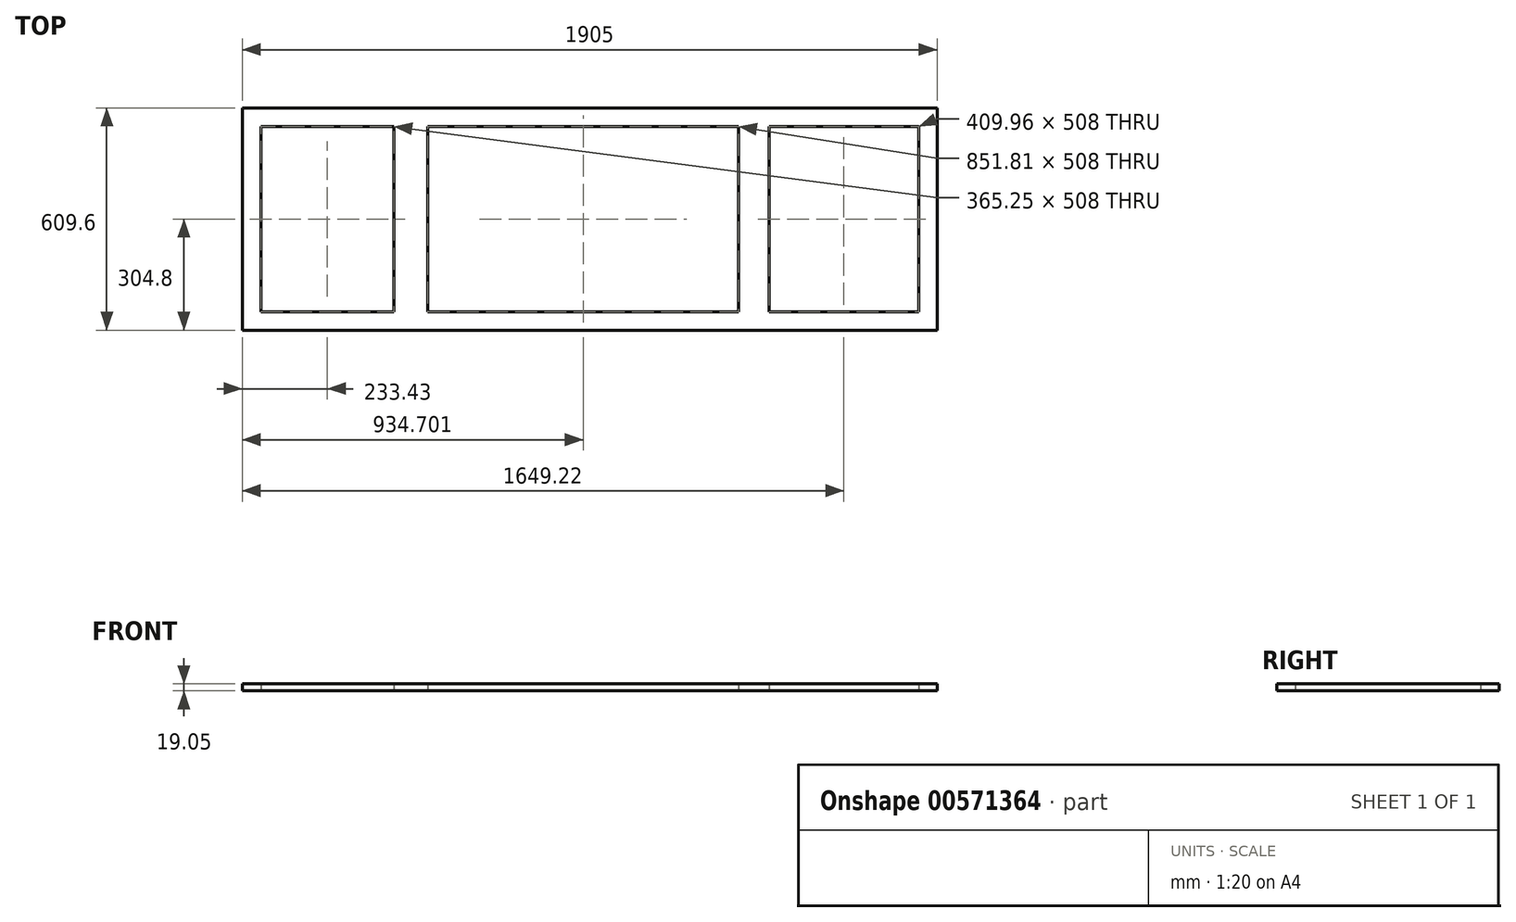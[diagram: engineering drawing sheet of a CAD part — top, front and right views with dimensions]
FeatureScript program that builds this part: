
annotation { "Feature Type Name" : "Feature", "Feature Type Description" : "" }
export const myFeature = defineFeature(function(context is Context, id is Id, definition is map)
    precondition{}
    {
        {
            var Q0;
            Q0=qCreatedBy(makeId("Top.planeOp"),FACE);
            var sketch = newSketch(context, id + "F0", { "sketchPlane" : qUnion([Q0])});
            skLineSegment(sketch, "E0", {"start": v(-940.37, 50.8) * mm, "end": v(964.63, 50.8) * mm});
            skLineSegment(sketch, "E1", {"start": v(-940.37, 50.8) * mm, "end": v(-940.37, 0) * mm});
            skLineSegment(sketch, "E2", {"start": v(-940.37, 0) * mm, "end": v(964.63, 0) * mm});
            skLineSegment(sketch, "E3", {"start": v(964.63, 0) * mm, "end": v(964.63, 50.8) * mm});
            skSolve(sketch);
        }
        {
            var Q0;
            Q0=makeQuery(id+"F0.imprint","IMPRINT",FACE,{"disambiguationData":[TD([[makeQuery(id+"F0.imprint","IMPRINT",EDGE,{"derivedFrom":sQuery(id+"F0.wireOp",EDGE,"E0")}),-1.0]])]});
            extrude(context, id + "F1", {"entities" : qUnion([Q0]), "depth" : 19.05 * mm, "offsetDistance" : 25.4 * mm});
        }
        {
            var Q0;
            Q0=makeQuery(id+"F1.opExtrude","SWEPT_FACE",FACE,{"disambiguationData":[OSD([sQuery(id+"F0.wireOp",EDGE,"E2")])]});
            var sketch = newSketch(context, id + "F2", { "sketchPlane" : qUnion([Q0])});
            skLineSegment(sketch, "E4.bottom", {"start": v(-940.37, 19.05) * mm, "end": v(-889.57, 19.05) * mm});
            skLineSegment(sketch, "E4.top", {"start": v(-940.37, 0) * mm, "end": v(-889.57, 0) * mm});
            skLineSegment(sketch, "E4.left", {"start": v(-940.37, 19.05) * mm, "end": v(-940.37, 0) * mm});
            skLineSegment(sketch, "E4.right", {"start": v(-889.57, 19.05) * mm, "end": v(-889.57, 0) * mm});
            skLineSegment(sketch, "E5.bottom", {"start": v(964.63, 19.05) * mm, "end": v(913.83, 19.05) * mm});
            skLineSegment(sketch, "E5.top", {"start": v(964.63, 0) * mm, "end": v(913.83, 0) * mm});
            skLineSegment(sketch, "E5.left", {"start": v(964.63, 19.05) * mm, "end": v(964.63, 0) * mm});
            skLineSegment(sketch, "E5.right", {"start": v(913.83, 19.05) * mm, "end": v(913.83, 0) * mm});
            skSolve(sketch);
        }
        {
            var Q0;
            Q0=makeQuery(id+"F2.imprint","IMPRINT",FACE,{"disambiguationData":[TD([[makeQuery(id+"F2.imprint","IMPRINT",EDGE,{"derivedFrom":sQuery(id+"F2.wireOp",EDGE,"E4.bottom")}),-1.0]])]});
            var Q1;
            Q1=makeQuery(id+"F2.imprint","IMPRINT",FACE,{"disambiguationData":[TD([[makeQuery(id+"F2.imprint","IMPRINT",EDGE,{"derivedFrom":sQuery(id+"F2.wireOp",EDGE,"E5.bottom")}),-1.0]])]});
            extrude(context, id + "F3", {"entities" : qUnion([Q0, Q1]), "operationType" : NewBodyOperationType.ADD, "depth" : 558.8 * mm, "offsetDistance" : 25.4 * mm});
        }
        {
            var Q0;
            Q0=makeQuery(id+"F3.opExtrude","SWEPT_FACE",FACE,{"disambiguationData":[OSD([sQuery(id+"F2.wireOp",EDGE,"E4.right")])]});
            var sketch = newSketch(context, id + "F4", { "sketchPlane" : qUnion([Q0])});
            skLineSegment(sketch, "E6.bottom", {"start": v(-558.8, 19.05) * mm, "end": v(-508, 19.05) * mm});
            skLineSegment(sketch, "E6.top", {"start": v(-558.8, 0) * mm, "end": v(-508, 0) * mm});
            skLineSegment(sketch, "E6.left", {"start": v(-558.8, 19.05) * mm, "end": v(-558.8, 0) * mm});
            skLineSegment(sketch, "E6.right", {"start": v(-508, 19.05) * mm, "end": v(-508, 0) * mm});
            skSolve(sketch);
        }
        {
            var Q0;
            Q0=makeQuery(id+"F4.imprint","IMPRINT",FACE,{"disambiguationData":[TD([[makeQuery(id+"F4.imprint","IMPRINT",EDGE,{"derivedFrom":sQuery(id+"F4.wireOp",EDGE,"E6.bottom")}),-1.0]])]});
            extrude(context, id + "F5", {"entities" : qUnion([Q0]), "operationType" : NewBodyOperationType.ADD, "depth" : 1854.2 * mm, "offsetDistance" : 25.4 * mm});
        }
        {
            var Q0;
            Q0=makeQuery(id+"F1.opExtrude","SWEPT_FACE",FACE,{"disambiguationData":[OSD([sQuery(id+"F0.wireOp",EDGE,"E2")])]});
            var sketch = newSketch(context, id + "F6", { "sketchPlane" : qUnion([Q0])});
            skLineSegment(sketch, "E7.bottom", {"start": v(-524.31, 19.05) * mm, "end": v(-431.58, 19.05) * mm});
            skLineSegment(sketch, "E7.top", {"start": v(-524.31, 0) * mm, "end": v(-431.58, 0) * mm});
            skLineSegment(sketch, "E7.left", {"start": v(-524.31, 19.05) * mm, "end": v(-524.31, 0) * mm});
            skLineSegment(sketch, "E7.right", {"start": v(-431.58, 19.05) * mm, "end": v(-431.58, 0) * mm});
            skLineSegment(sketch, "E8.bottom", {"start": v(420.24, 19.05) * mm, "end": v(503.87, 19.05) * mm});
            skLineSegment(sketch, "E8.top", {"start": v(420.24, 0) * mm, "end": v(503.87, 0) * mm});
            skLineSegment(sketch, "E8.left", {"start": v(420.24, 19.05) * mm, "end": v(420.24, 0) * mm});
            skLineSegment(sketch, "E8.right", {"start": v(503.87, 19.05) * mm, "end": v(503.87, 0) * mm});
            skSolve(sketch);
        }
        {
            var Q0;
            Q0=makeQuery(id+"F6.imprint","IMPRINT",FACE,{"disambiguationData":[TD([[makeQuery(id+"F6.imprint","IMPRINT",EDGE,{"derivedFrom":sQuery(id+"F6.wireOp",EDGE,"E8.bottom")}),-1.0]])]});
            var Q1;
            Q1=makeQuery(id+"F6.imprint","IMPRINT",FACE,{"disambiguationData":[TD([[makeQuery(id+"F6.imprint","IMPRINT",EDGE,{"derivedFrom":sQuery(id+"F6.wireOp",EDGE,"E7.bottom")}),-1.0]])]});
            extrude(context, id + "F7", {"entities" : qUnion([Q0, Q1]), "operationType" : NewBodyOperationType.ADD, "depth" : 558.8 * mm, "offsetDistance" : 25.4 * mm});
        }
    });
